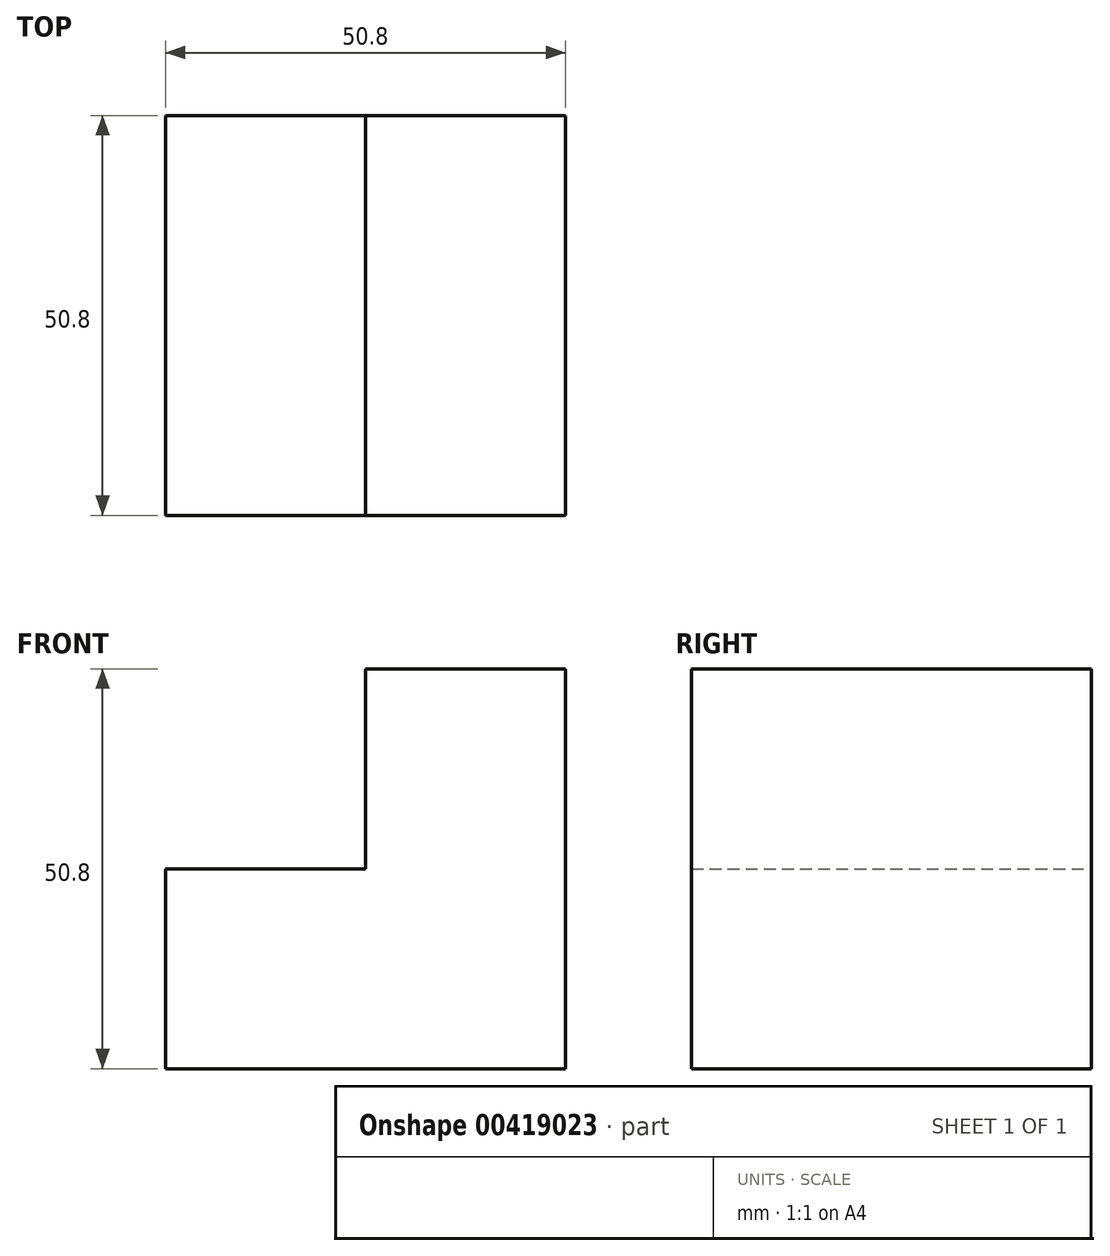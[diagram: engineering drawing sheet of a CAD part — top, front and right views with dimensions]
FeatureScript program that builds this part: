
annotation { "Feature Type Name" : "Feature", "Feature Type Description" : "" }
export const myFeature = defineFeature(function(context is Context, id is Id, definition is map)
    precondition{}
    {
        {
            var Q0;
            Q0=qCreatedBy(makeId("Front.planeOp"),FACE);
            var sketch = newSketch(context, id + "F0", { "sketchPlane" : qUnion([Q0])});
            skLineSegment(sketch, "E0", {"start": v(0, 0) * mm, "end": v(0, 50.8) * mm});
            skLineSegment(sketch, "E1", {"start": v(0, 0) * mm, "end": v(-50.8, 0) * mm});
            skLineSegment(sketch, "E2", {"start": v(-50.8, 0) * mm, "end": v(-50.8, 25.4) * mm});
            skLineSegment(sketch, "E3", {"start": v(-50.8, 25.4) * mm, "end": v(-25.4, 25.4) * mm});
            skLineSegment(sketch, "E4", {"start": v(-25.4, 25.4) * mm, "end": v(-25.4, 50.8) * mm});
            skLineSegment(sketch, "E5", {"start": v(-25.4, 50.8) * mm, "end": v(0, 50.8) * mm});
            skSolve(sketch);
        }
        {
            var Q0;
            Q0=makeQuery(id+"F0.imprint","IMPRINT",FACE,{"disambiguationData":[TD([[makeQuery(id+"F0.imprint","IMPRINT",EDGE,{"derivedFrom":sQuery(id+"F0.wireOp",EDGE,"E0")}),1.0]])]});
            extrude(context, id + "F1", {"entities" : qUnion([Q0]), "depth" : 50.8 * mm});
        }
    });
